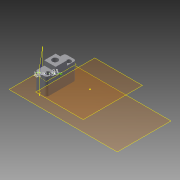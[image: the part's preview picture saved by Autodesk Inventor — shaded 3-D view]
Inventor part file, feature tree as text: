
AUTODESK INVENTOR PART (.ipt)
format: ipt  version: 2015 (Build 190159000, 159)  size: 143,360 bytes
history: native  units: mm
features: plane x4, sketch x3, reference x3, extrude x2, hole x2, fillet x1, projected_geometry x1
ambient origin geometry x8: Origin, YZ Plane, XZ Plane, XY Plane, X Axis, Y Axis, Z Axis, Center Point
bodies: Solid1 (feature_tree)
feature tree (16):
  plane  "Work Plane1"
  plane  "Work Plane2"
  extrude  "Extrusion1"  Depth=15.0mm
  plane  "Work Plane3"
  sketch  "Sketch4"  dims[d1=15.0mm d2=0.0mm d7=22.68928mm]
  plane  "Work Plane6"
  sketch  "Sketch7"  dims[d8=1.5mm d9=1.5mm]
  hole  "Hole1"  [1 undecoded]
  hole  "Hole2"  [1 undecoded]
  extrude  "Extrusion2"  Depth=2.0mm
  fillet  "Fillet1"  Radius=4.0mm
  reference  "Reference1"
  reference  "Reference2"
  reference  "Reference3"
  projected_geometry  "Projected Loop1"
  sketch  "Sketch9"  dims[d10=0.5mm d13=1.5mm d17=2.459mm d18=6.0mm d19=4.0mm d20=2.0mm d21=90.0deg d22=8.0mm d23=20.594885mm d24=2.459mm d25=6.0mm d26=4.0mm d27=2.0mm d28=90.0deg d29=8.0mm d30=20.594885mm d31=2.5mm d32=4.0mm d33=8.0mm d34=10.0mm d35=0.0mm d36=2.0mm d37=26.0mm]
note: 2 required parameter values undecoded (feature->parameter linkage not recoverable at this tier; creation-order binding heuristic only, values carry confidence <= 0.55)
